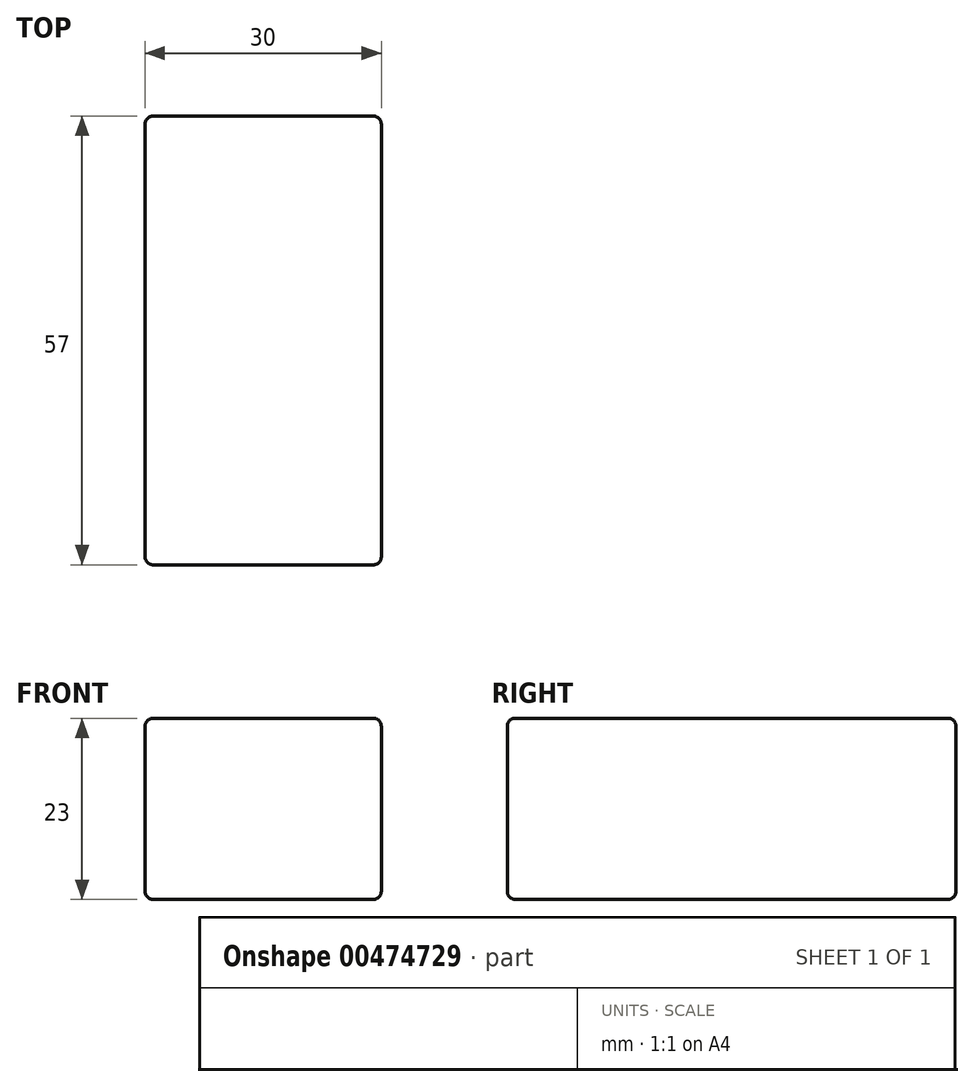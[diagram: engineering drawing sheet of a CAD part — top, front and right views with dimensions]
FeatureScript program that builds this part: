
annotation { "Feature Type Name" : "Feature", "Feature Type Description" : "" }
export const myFeature = defineFeature(function(context is Context, id is Id, definition is map)
    precondition{}
    {
        {
            var Q0;
            Q0=qCreatedBy(makeId("Top.planeOp"),FACE);
            var sketch = newSketch(context, id + "F0", { "sketchPlane" : qUnion([Q0])});
            skLineSegment(sketch, "E0.bottom", {"start": v(0, 0) * mm, "end": v(30, 0) * mm});
            skLineSegment(sketch, "E0.top", {"start": v(0, 57) * mm, "end": v(30, 57) * mm});
            skLineSegment(sketch, "E0.left", {"start": v(0, 0) * mm, "end": v(0, 57) * mm});
            skLineSegment(sketch, "E0.right", {"start": v(30, 0) * mm, "end": v(30, 57) * mm});
            skSolve(sketch);
        }
        {
            var Q0;
            Q0 = qSketchRegion(id + "F0", true);
            extrude(context, id + "F1", {"entities" : qUnion([Q0]), "depth" : 23 * mm, "offsetDistance" : 25 * mm});
        }
        {
            var Q0;
            Q0=makeQuery(id+"F1.opExtrude","CAP_EDGE",EDGE,{"disambiguationData":[OSD([sQuery(id+"F0.wireOp",EDGE,"E0.bottom")])],"isStart":false});
            var Q1;
            Q1=makeQuery(id+"F1.opExtrude","CAP_EDGE",EDGE,{"disambiguationData":[OSD([sQuery(id+"F0.wireOp",EDGE,"E0.left")])],"isStart":false});
            var Q2;
            Q2=makeQuery(id+"F1.opExtrude","CAP_EDGE",EDGE,{"disambiguationData":[OSD([sQuery(id+"F0.wireOp",EDGE,"E0.left")])],"isStart":true});
            var Q3;
            Q3=makeQuery(id+"F1.opExtrude","SWEPT_EDGE",EDGE,{"disambiguationData":[OSD([sQuery(id+"F0.wireOp",EDGE,"E0.bottom"),sQuery(id+"F0.wireOp",EDGE,"E0.left")])]});
            var Q4;
            Q4=makeQuery(id+"F1.opExtrude","CAP_EDGE",EDGE,{"disambiguationData":[OSD([sQuery(id+"F0.wireOp",EDGE,"E0.bottom")])],"isStart":true});
            var Q5;
            Q5=makeQuery(id+"F1.opExtrude","SWEPT_EDGE",EDGE,{"disambiguationData":[OSD([sQuery(id+"F0.wireOp",EDGE,"E0.bottom"),sQuery(id+"F0.wireOp",EDGE,"E0.right")])]});
            var Q6;
            Q6=makeQuery(id+"F1.opExtrude","CAP_EDGE",EDGE,{"disambiguationData":[OSD([sQuery(id+"F0.wireOp",EDGE,"E0.right")])],"isStart":false});
            var Q7;
            Q7=makeQuery(id+"F1.opExtrude","CAP_FACE",FACE,{"disambiguationData":[OSD([sQuery(id+"F0.wireOp",EDGE,"E0.bottom"),sQuery(id+"F0.wireOp",EDGE,"E0.top"),sQuery(id+"F0.wireOp",EDGE,"E0.left"),sQuery(id+"F0.wireOp",EDGE,"E0.right")])],"isStart":true});
            var Q8;
            Q8=makeQuery(id+"F1.opExtrude","SWEPT_EDGE",EDGE,{"disambiguationData":[OSD([sQuery(id+"F0.wireOp",EDGE,"E0.top"),sQuery(id+"F0.wireOp",EDGE,"E0.right")])]});
            var Q9;
            Q9=makeQuery(id+"F1.opExtrude","CAP_EDGE",EDGE,{"disambiguationData":[OSD([sQuery(id+"F0.wireOp",EDGE,"E0.top")])],"isStart":false});
            var Q10;
            Q10=makeQuery(id+"F1.opExtrude","SWEPT_EDGE",EDGE,{"disambiguationData":[OSD([sQuery(id+"F0.wireOp",EDGE,"E0.top"),sQuery(id+"F0.wireOp",EDGE,"E0.left")])]});
            fillet(context, id + "F2", {"entities" : qUnion([Q0, Q1, Q2, Q3, Q4, Q5, Q6, Q7, Q8, Q9, Q10]), "radius" : 1 * mm, "tangentPropagation" : true, "allowEdgeOverflow" : false});
        }
    });
